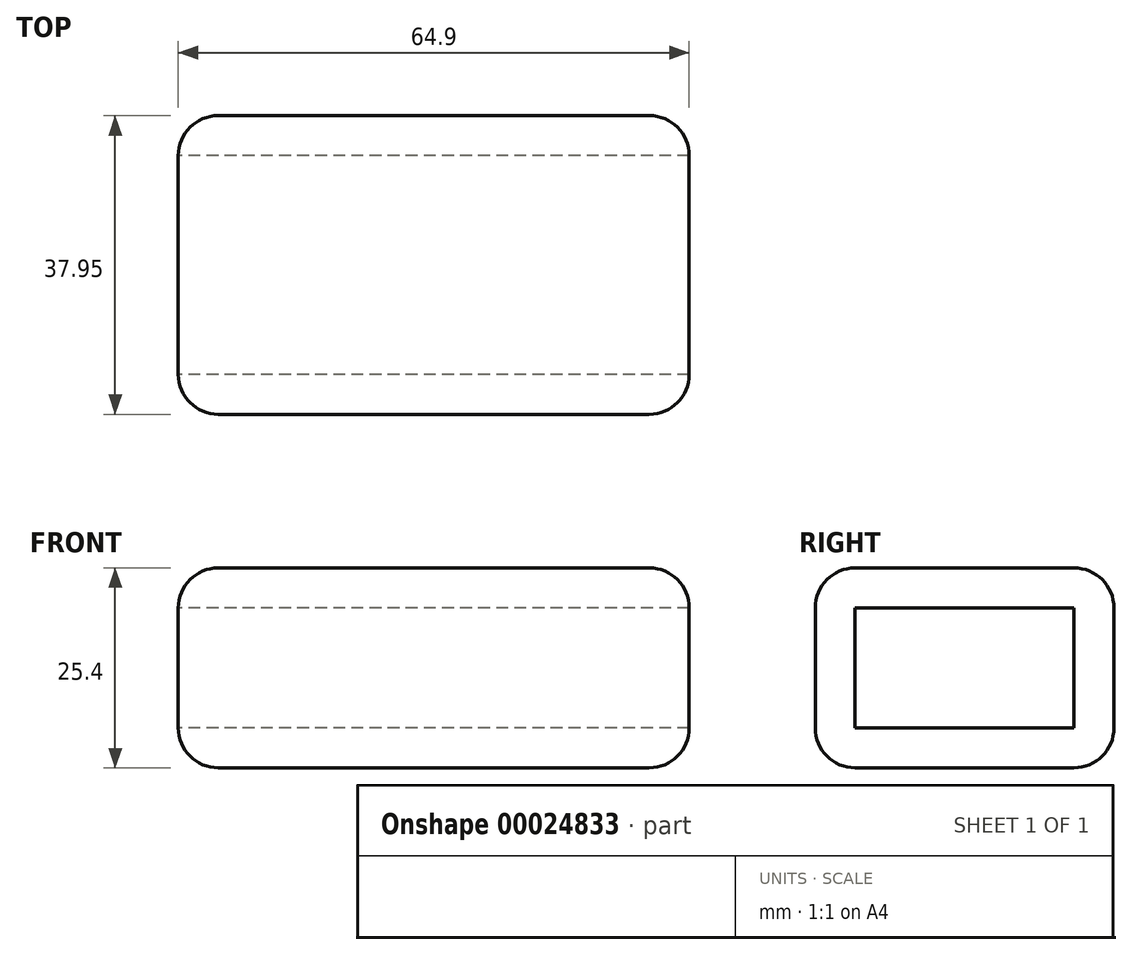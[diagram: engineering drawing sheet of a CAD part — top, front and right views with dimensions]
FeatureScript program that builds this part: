
annotation { "Feature Type Name" : "Feature", "Feature Type Description" : "" }
export const myFeature = defineFeature(function(context is Context, id is Id, definition is map)
    precondition{}
    {
        {
            var Q0;
            Q0=qCreatedBy(makeId("Top.planeOp"),FACE);
            var sketch = newSketch(context, id + "F0", { "sketchPlane" : qUnion([Q0])});
            skLineSegment(sketch, "E0.bottom", {"start": v(-120.9, -23.09) * mm, "end": v(-56, -23.09) * mm});
            skLineSegment(sketch, "E0.top", {"start": v(-120.9, 14.86) * mm, "end": v(-56, 14.86) * mm});
            skLineSegment(sketch, "E0.left", {"start": v(-120.9, -23.09) * mm, "end": v(-120.9, 14.86) * mm});
            skLineSegment(sketch, "E0.right", {"start": v(-56, -23.09) * mm, "end": v(-56, 14.86) * mm});
            skSolve(sketch);
        }
        {
            var Q0;
            Q0=makeQuery(id+"F0.imprint","IMPRINT",FACE,{"disambiguationData":[TD([[makeQuery(id+"F0.imprint","IMPRINT",EDGE,{"derivedFrom":sQuery(id+"F0.wireOp",EDGE,"E0.bottom")}),1.0]])]});
            extrude(context, id + "F1", {"entities" : qUnion([Q0]), "depth" : 25.4 * mm});
        }
        {
            var Q0;
            Q0=makeQuery(id+"F1.opExtrude","CAP_EDGE",EDGE,{"disambiguationData":[OSD([sQuery(id+"F0.wireOp",EDGE,"E0.bottom")])],"isStart":false});
            var Q1;
            Q1=makeQuery(id+"F1.opExtrude","CAP_EDGE",EDGE,{"disambiguationData":[OSD([sQuery(id+"F0.wireOp",EDGE,"E0.left")])],"isStart":false});
            var Q2;
            Q2=makeQuery(id+"F1.opExtrude","CAP_EDGE",EDGE,{"disambiguationData":[OSD([sQuery(id+"F0.wireOp",EDGE,"E0.top")])],"isStart":false});
            var Q3;
            Q3=makeQuery(id+"F1.opExtrude","CAP_EDGE",EDGE,{"disambiguationData":[OSD([sQuery(id+"F0.wireOp",EDGE,"E0.right")])],"isStart":false});
            var Q4;
            Q4=makeQuery(id+"F1.opExtrude","SWEPT_EDGE",EDGE,{"disambiguationData":[OSD([sQuery(id+"F0.wireOp",EDGE,"E0.bottom"),sQuery(id+"F0.wireOp",EDGE,"E0.right")])]});
            var Q5;
            Q5=makeQuery(id+"F1.opExtrude","SWEPT_EDGE",EDGE,{"disambiguationData":[OSD([sQuery(id+"F0.wireOp",EDGE,"E0.top"),sQuery(id+"F0.wireOp",EDGE,"E0.right")])]});
            var Q6;
            Q6=makeQuery(id+"F1.opExtrude","SWEPT_EDGE",EDGE,{"disambiguationData":[OSD([sQuery(id+"F0.wireOp",EDGE,"E0.bottom"),sQuery(id+"F0.wireOp",EDGE,"E0.left")])]});
            var Q7;
            Q7=makeQuery(id+"F1.opExtrude","CAP_EDGE",EDGE,{"disambiguationData":[OSD([sQuery(id+"F0.wireOp",EDGE,"E0.bottom")])],"isStart":true});
            var Q8;
            Q8=makeQuery(id+"F1.opExtrude","CAP_EDGE",EDGE,{"disambiguationData":[OSD([sQuery(id+"F0.wireOp",EDGE,"E0.right")])],"isStart":true});
            var Q9;
            Q9=makeQuery(id+"F1.opExtrude","CAP_EDGE",EDGE,{"disambiguationData":[OSD([sQuery(id+"F0.wireOp",EDGE,"E0.left")])],"isStart":true});
            var Q10;
            Q10=makeQuery(id+"F1.opExtrude","CAP_EDGE",EDGE,{"disambiguationData":[OSD([sQuery(id+"F0.wireOp",EDGE,"E0.top")])],"isStart":true});
            var Q11;
            Q11=makeQuery(id+"F1.opExtrude","SWEPT_EDGE",EDGE,{"disambiguationData":[OSD([sQuery(id+"F0.wireOp",EDGE,"E0.top"),sQuery(id+"F0.wireOp",EDGE,"E0.left")])]});
            fillet(context, id + "F2", {"entities" : qUnion([Q0, Q1, Q2, Q3, Q4, Q5, Q6, Q7, Q8, Q9, Q10, Q11]), "radius" : 5.08 * mm, "tangentPropagation" : true, "allowEdgeOverflow" : false});
        }
        {
            var Q0;
            Q0=makeQuery(id+"F1.opExtrude","SWEPT_FACE",FACE,{"disambiguationData":[OSD([sQuery(id+"F0.wireOp",EDGE,"E0.left")])]});
            var sketch = newSketch(context, id + "F3", { "sketchPlane" : qUnion([Q0])});
            skSolve(sketch);
        }
        {
            var Q0;
            {var subQ0=sQuery(id+"F0.wireOp",EDGE,"E0.left");var subQ1=makeQuery(id+"F1.opExtrude","SWEPT_FACE",FACE,{"disambiguationData":[OSD([subQ0])]});Q0=makeQuery(id+"F3.imprint","IMPRINT",FACE,{"disambiguationData":[TD([[makeQuery(id+"F3.imprint","IMPRINT",EDGE,{"derivedFrom":makeQuery(id+"F2.opFillet","BLEND_EDGE",EDGE,{"blendedFrom":[makeQuery(id+"F1.opExtrude","CAP_EDGE",EDGE,{"disambiguationData":[OSD([subQ0])],"isStart":true}),subQ1],"blendedInto":[subQ1]})}),1.0]])]});}
            extrude(context, id + "F4", {"entities" : qUnion([Q0]), "operationType" : NewBodyOperationType.REMOVE, "endBound" : BoundingType.THROUGH_ALL, "oppositeDirection" : true, "depth" : 25.4 * mm});
        }
    });
